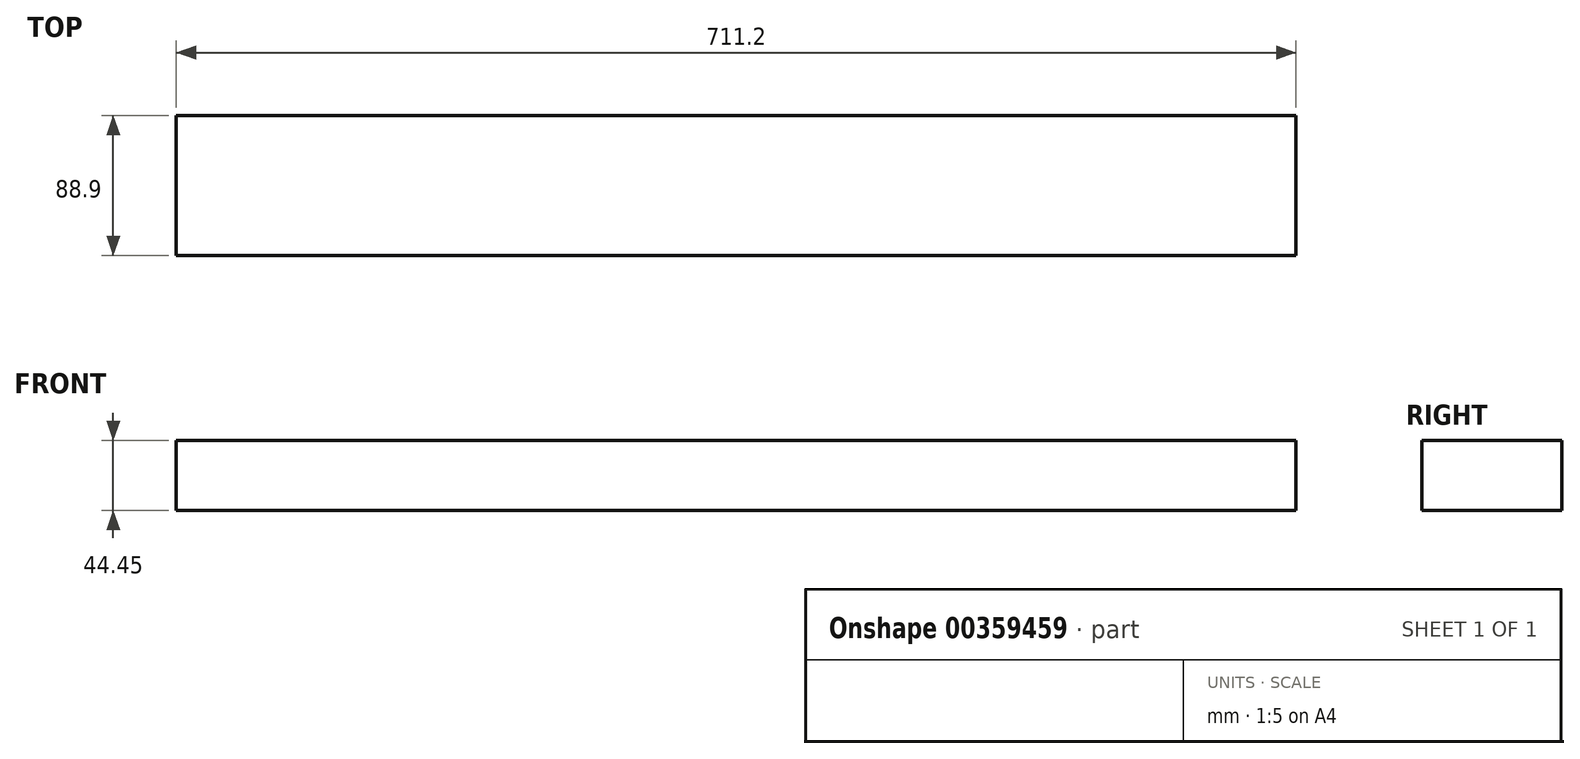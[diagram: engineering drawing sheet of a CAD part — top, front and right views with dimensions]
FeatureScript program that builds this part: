
annotation { "Feature Type Name" : "Feature", "Feature Type Description" : "" }
export const myFeature = defineFeature(function(context is Context, id is Id, definition is map)
    precondition{}
    {
        {
            var Q0;
            Q0=qCreatedBy(makeId("Front.planeOp"),FACE);
            var sketch = newSketch(context, id + "F0", { "sketchPlane" : qUnion([Q0])});
            skLineSegment(sketch, "E0.bottom", {"start": v(0, 0) * mm, "end": v(711.2, 0) * mm});
            skLineSegment(sketch, "E0.top", {"start": v(0, 44.45) * mm, "end": v(711.2, 44.45) * mm});
            skLineSegment(sketch, "E0.left", {"start": v(0, 0) * mm, "end": v(0, 44.45) * mm});
            skLineSegment(sketch, "E0.right", {"start": v(711.2, 0) * mm, "end": v(711.2, 44.45) * mm});
            skSolve(sketch);
        }
        {
            var Q0;
            Q0=makeQuery(id+"F0.imprint","IMPRINT",FACE,{"disambiguationData":[TD([[makeQuery(id+"F0.imprint","IMPRINT",EDGE,{"derivedFrom":sQuery(id+"F0.wireOp",EDGE,"E0.bottom")}),1.0]])]});
            extrude(context, id + "F1", {"entities" : qUnion([Q0]), "depth" : 88.9 * mm});
        }
    });
